# Revit family: 93002009(2023)
name_source: partatom
category: Plumbing Fixtures
units: mm (PartAtom-declared; Revit-internal decimal feet)

## family parameters
Always vertical = Yes
Cut with Voids When Loaded = No
OmniClass Number = 23.45.55.00
OmniClass Title = Sanitary Faucets, Wastes
Part Type = Normal
Room Calculation Point = No
Round Connector Dimension = Use Diameter
Shared = No
Work Plane-Based = No

## types (1)
- 93002009 HANSAELECTRA
    2D/3D/BIM Files URL = http://static.hansa.com
    3D View = https://static.hansa.com
    Advanced Features = 3S-installation system for safe and simple mounting;Software settings adjustable via App
    Aerator = PCA® - constant flow rate regardless of pressure variations;Adjustable flow angle
    Afterflow Period = 3 s (1-20 s)
    AssetType = Fixed
    Automatic Flush Frequency = off (off/1-120 h)
    Automatic Flush Period = 30 s (1-1800 s)
    BIMObjectName = 93002009(2023)
    Backflow Prevention EN1717 = EB
    Bluetooth = 5.x (D060576)
    BodyMaterial = Brass
    Brand = HANSA
    CO2 Emissions (A1-A3) = 3.63
    CO2 Emissions (A4) = 0.14
    CO2 Emissions (C2) = 0.01
    CO2 Emissions (C3) = 0
    CO2 Emissions (C4) = 0.86
    CO2 Emissions (D) = -0.68
    Catalog Drawing URL = http://static.hansa.com
    CloseOffRating = 0
    Color = Chrome
    Connection = Flexible inlet pipes
    Connection Size = G3/8
    Default Elevation = 0 mm  [stored 0 ft]
    Dimension Drawing URL = http://static.hansa.com
    DurationUnit = Year
    EAN Number = 4057304019500
    EMC Directive = Radio Equipment Directive 2014/53/EU , 
Low Voltage Directive 2014/35/EU , 
EMC Directive 2014/30/EU , 
RoHS Directive 2011/65/EU
    EN Standard = EN 15091,
ETSI EN 301 489-1 V1.9.2 , 
ETSI EN 300 328 v2.2.2 , 
EN 61000-6-1:2007 , 
EN 61000-6-3:2007+A1:2011+AC:2012 , 
EN 60335-1:2012+A11+A13+A1+A14+A2+A15:2021, Part 19.11.4
    ETIM Class Number = EC010340 Electronic tap
    Electrical Connection = 230 / 9 V
    Electronic Parts = ;Power supply;Light indicated function(s)
    FDV Document URL = http://www.hansa.com
    FaucetMainMaterial = Brass
    Features = Washbasin faucet
    Finish = Polished
    FlowCoefficient = 0
    Group = Sales item
    IfcExportAs = IfcValveType
    IfcExportType = FAUCET
    InletConnectionSize = 10 mm  [stored 0.0328084 ft]
    Installation Type = Deck mounted
    Installation and Maintenance Guide URL = http://static.hansa.com
    Interactive AR View URL = https://static.hansa.com
    Lever Handle = Temperature control handle
    Long Marketing = Bluetooth Touchless faucet with tilt aerator. +/- 10° adjustment option.
Easy grip temperature lever for good grip and easy adjustment. 
SMART intelligent bluetooth sensor with 3 optical lenses for improved performance supported by app connection for personalized and easy adjustment of sensor settings.
Metal free waterways due to high pressure composite construction and easy installation due to fast and easy 3S installation system.
    Manufacturer = HANSA
    ManufacturerName = HANSA
    ManufacturerURL = http://www.hansa.com
    Market = International;Germany;Austria;Switzerland;Belgium;Netherlands;Italy
    Material = Composite
    Max Flow Period = 2 min (1 - 1800 s)
    Max. Hot Water Supply = 70 °C
    Mechanical Parts = Mixing valve for manual temperature control;Non-return valve(s);Litter filter(s)
    Mobile Product Information URL = http://mpi.hansa.com
    Model = 93002009 HANSAELECTRA
    ModelReference = 93002009
    Mounting Holes = 1 hole
    NBSDescription = Water supply fittings for wash basins and troughs
    NBSReference = 45-35-70/371
    Name = 93002009 HANSAELECTRA
    Name_en = 93002009 HANSAELECTRA
    Noise Class = I (ISO 3822)
    NominalDepth = 163 mm
    NominalHeight = 190 mm  [stored 0.62336 ft]
    NominalWidth = 68 mm
    Operating Distance = 20-130 mm (110/130/160 mm)
    Operating Voltage = 9 V
    Product Code = 93002009
    Product Family = null Touchless;Plug transformer;Bluetooth®;Lead free
    Product Image URL = http://static.hansa.com
    Product URL = http://static.hansa.com
    Protection Class = IP 55 / transformer IP 20
    Sales Package dimensions (LxWxH) = 568 x 182 x 78
    Shape = Sculptured
    Short Marketing = Electra 93 series is giving you a whole new modern design with its rounded square body and spout giving you new fresh and updated design.
The tall design compliments the new trends of modern bathroom of more square design and shallow sinks, where the extra height gives you more comfortable usage.

Key Features
Aerator with Tilt function +/- 10° for more flexible installation
Newest Sensor technology for better detection and operation comfort
Bluetooth technology for easy adjustment to personalize settings 
Power Plug
    Size = 70x165x190 mm
    Spout Projection = 118 mm
    Spout Type = Fixed spout
    Surface treatment = Chrome
    Technical DataSheet URL = http://www.hansa.com
    Temperature Adjustments = Adjustable hot water stop (included, retrofittable)
    UNSPSC Class Number = 30181700 Faucets or taps
    URL Declaration Of Performance (DOP) = http://static.hansa.com
    URL Declaration of Asbestos = http://static.hansa.com
    URL Declaration of Conformity = http://static.hansa.com
    URL Declaration of SCIP = http://static.hansa.com
    URL EU Packaging Declaration = http://static.hansa.com
    URL EcoLabel Declaration = http://static.hansa.com
    URL Environmental Product Declaration EPD = http://www.hansa.com Group EPD_Touchless composite washbasin faucet.pdf
    URL Materials Declaration = http://www.hansa.com
    URL REACH = http://static.hansa.com
    URL WEEE = http://static.hansa.com
    Uniclass2 = Pr_40_30_96_96
    Uniclass2015Description = Washbasin manual water supply sets
    Uniclass2015Reference = Pr_40_20_87_96
    Version = 1
    VersionDate = 20/02/2024
    Warranty Information URL = http://warranty.hansa.com
    WarrantyDescription = http://warranty.hansa.com
    WarrantyDurationUnit = Year
    Working Pressure = 100 - 1000 kPa

note: [stored X ft] marks values corroborated as IEEE doubles in the binary element streams (Revit-internal decimal feet)

## geometry (parser evidence)
native form markers: Sweep x7
no freeform markers — native parametric forms only
